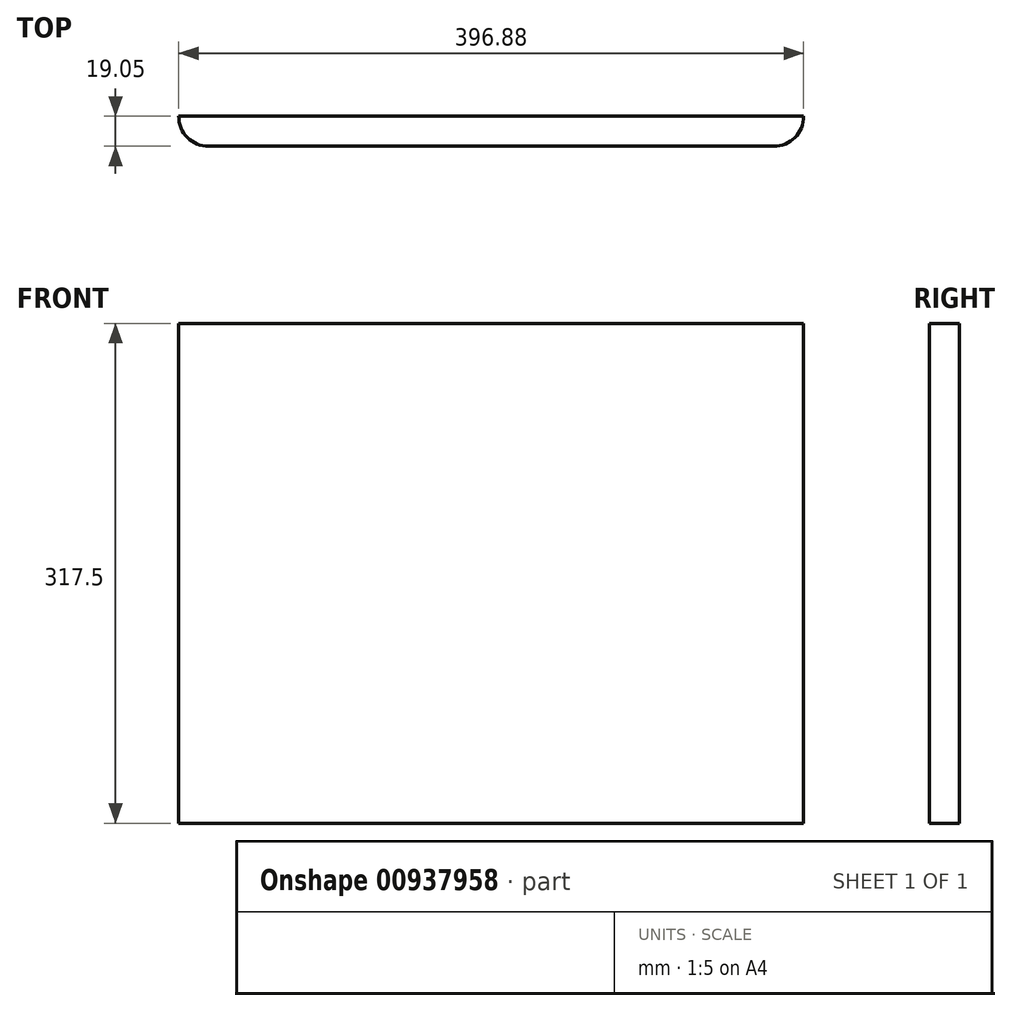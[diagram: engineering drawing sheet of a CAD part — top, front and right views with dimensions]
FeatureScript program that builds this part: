
annotation { "Feature Type Name" : "Feature", "Feature Type Description" : "" }
export const myFeature = defineFeature(function(context is Context, id is Id, definition is map)
    precondition{}
    {
        {
            var Q0;
            Q0=qCreatedBy(makeId("Front.planeOp"),FACE);
            var sketch = newSketch(context, id + "F0", { "sketchPlane" : qUnion([Q0])});
            skLineSegment(sketch, "E0.bottom", {"start": v(198.44, 158.75) * mm, "end": v(-198.44, 158.75) * mm});
            skLineSegment(sketch, "E0.top", {"start": v(198.44, -158.75) * mm, "end": v(-198.44, -158.75) * mm});
            skLineSegment(sketch, "E0.left", {"start": v(198.44, 158.75) * mm, "end": v(198.44, -158.75) * mm});
            skLineSegment(sketch, "E0.right", {"start": v(-198.44, 158.75) * mm, "end": v(-198.44, -158.75) * mm});
            skPoint(sketch, "E0.middle", {"position": v(0, 0) * mm});
            skSolve(sketch);
        }
        {
            var Q0;
            Q0=makeQuery(id+"F0.imprint","IMPRINT",FACE,{"disambiguationData":[TD([[makeQuery(id+"F0.imprint","IMPRINT",EDGE,{"derivedFrom":sQuery(id+"F0.wireOp",EDGE,"E0.bottom")}),1.0]])]});
            extrude(context, id + "F1", {"entities" : qUnion([Q0]), "depth" : 19.05 * mm, "offsetDistance" : 25.4 * mm});
        }
        {
            var Q0;
            Q0=makeQuery(id+"F1.opExtrude","CAP_EDGE",EDGE,{"disambiguationData":[OSD([sQuery(id+"F0.wireOp",EDGE,"E0.right")])],"isStart":false});
            var Q1;
            Q1=makeQuery(id+"F1.opExtrude","CAP_EDGE",EDGE,{"disambiguationData":[OSD([sQuery(id+"F0.wireOp",EDGE,"E0.left")])],"isStart":false});
            fillet(context, id + "F2", {"entities" : qUnion([Q0, Q1]), "radius" : 19.05 * mm, "tangentPropagation" : true, "allowEdgeOverflow" : false});
        }
    });
